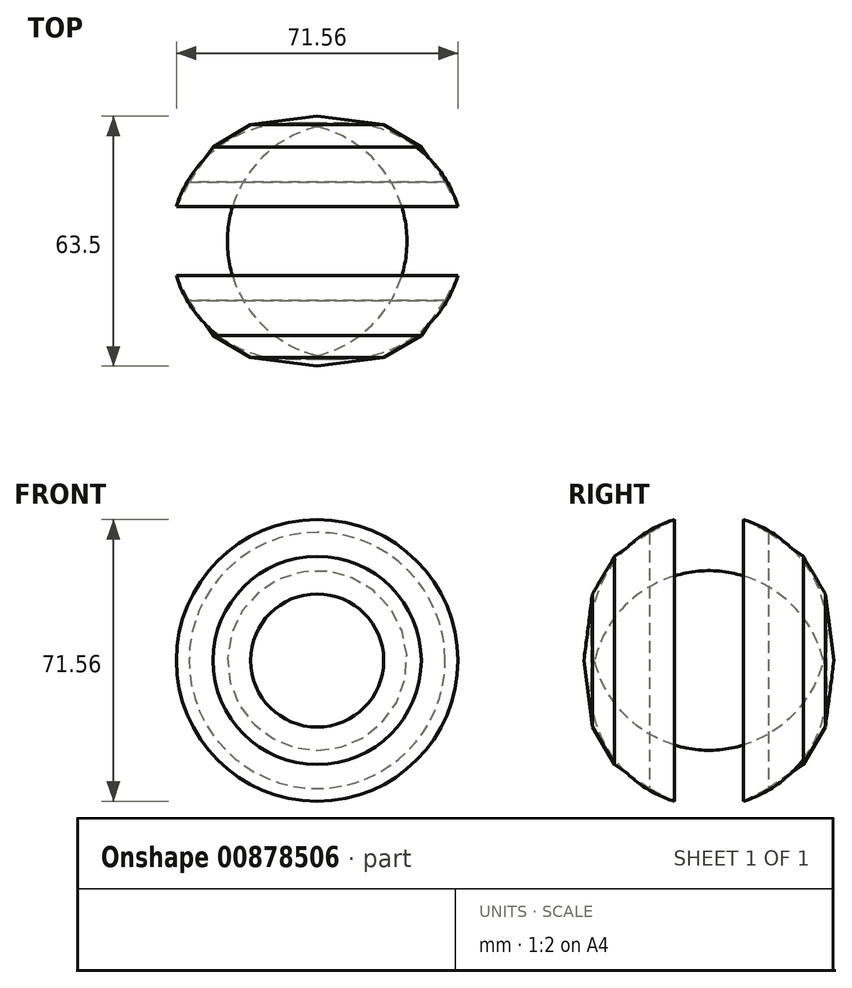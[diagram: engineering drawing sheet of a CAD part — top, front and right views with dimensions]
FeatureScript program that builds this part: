
annotation { "Feature Type Name" : "Feature", "Feature Type Description" : "" }
export const myFeature = defineFeature(function(context is Context, id is Id, definition is map)
    precondition{}
    {
        {
            var Q0;
            Q0=qCreatedBy(makeId("Top.planeOp"),FACE);
            var sketch = newSketch(context, id + "F0", { "sketchPlane" : qUnion([Q0])});
            skLineSegment(sketch, "E0", {"start": v(0, 31.75) * mm, "end": v(0, -31.75) * mm});
            skLineSegment(sketch, "E1", {"start": v(0, 31.75) * mm, "end": v(16.91, 29.6) * mm});
            skLineSegment(sketch, "E2", {"start": v(16.91, 29.6) * mm, "end": v(26.45, 23.96) * mm});
            skLineSegment(sketch, "E3", {"start": v(26.45, 23.96) * mm, "end": v(32.52, 15.07) * mm});
            skLineSegment(sketch, "E4", {"start": v(32.52, 15.07) * mm, "end": v(35.78, 8.78) * mm});
            skLineSegment(sketch, "E5", {"start": v(35.78, 8.78) * mm, "end": v(35.78, 0) * mm});
            skLineSegment(sketch, "E6", {"start": v(35.78, 0) * mm, "end": v(0, 0) * mm});
            skLineSegment(sketch, "E7.MirrorCS", {"start": v(32.52, -15.07) * mm, "end": v(35.78, -8.78) * mm});
            skLineSegment(sketch, "E8.MirrorCS", {"start": v(35.78, -8.78) * mm, "end": v(35.78, 0) * mm});
            skLineSegment(sketch, "E9.MirrorCS", {"start": v(0, -31.75) * mm, "end": v(16.91, -29.6) * mm});
            skLineSegment(sketch, "E10.MirrorCS", {"start": v(26.45, -23.96) * mm, "end": v(32.52, -15.07) * mm});
            skLineSegment(sketch, "E11.MirrorCS", {"start": v(16.91, -29.6) * mm, "end": v(26.45, -23.96) * mm});
            skArc(sketch, "E12", {"start": v(35.78, -8.78) * mm, "mid": v(37.1, 0) * mm, "end": v(35.78, 8.78) * mm});
            skSolve(sketch);
        }
        {
            var Q0;
            Q0 = qSketchRegion(id + "F0", true);
            var Q1;
            Q1=sQuery(id+"F0.wireOp",EDGE,"E0");
            revolve(context, id + "F1", {"surfaceOperationType" : NewSurfaceOperationType.NEW, "entities" : qUnion([Q0]), "axis" : qUnion([Q1]), "revolveType" : RevolveType.FULL});
        }
    });
